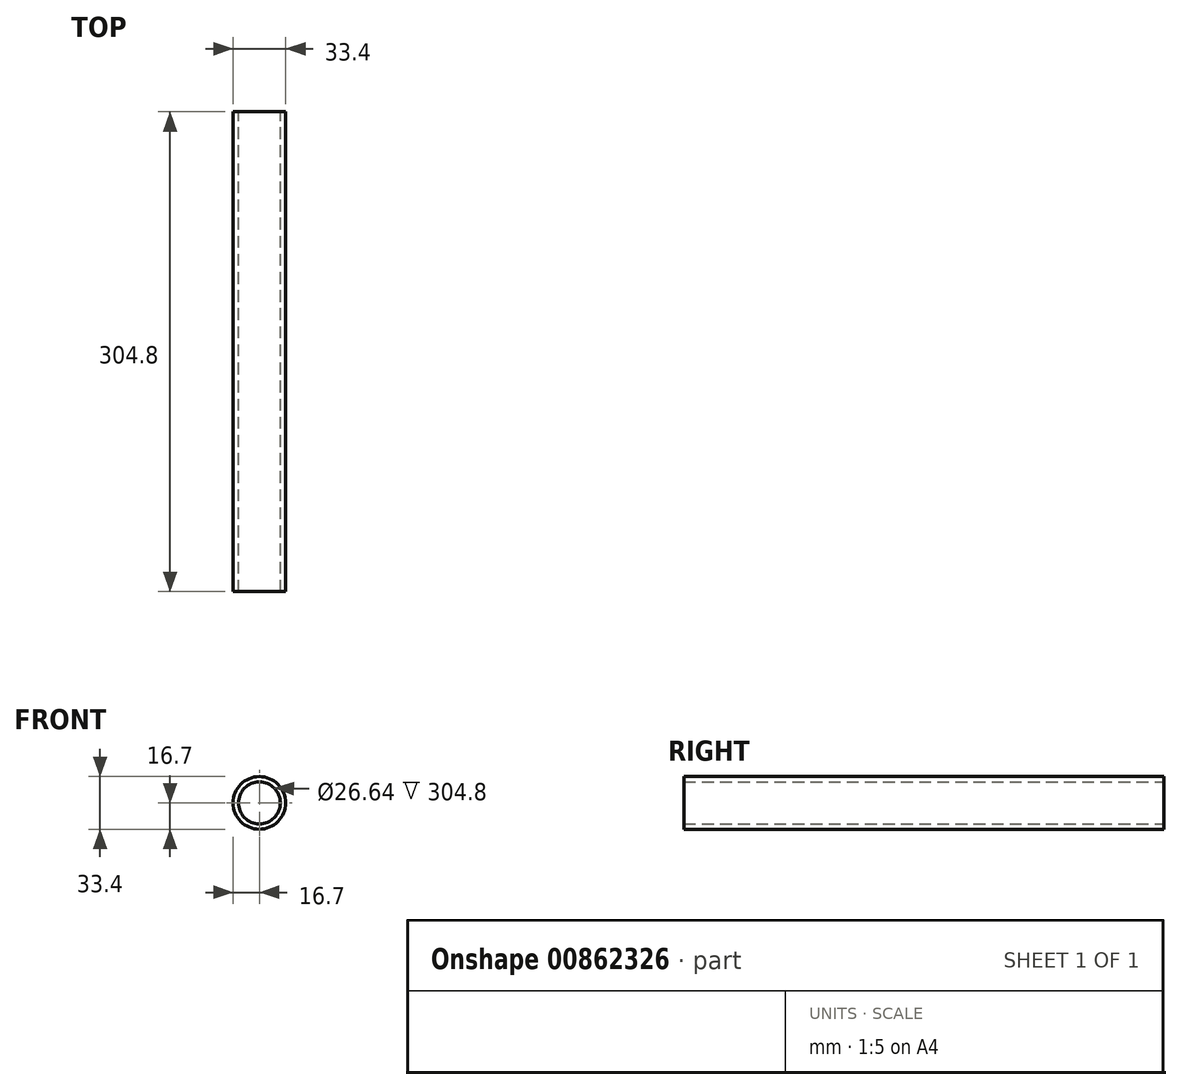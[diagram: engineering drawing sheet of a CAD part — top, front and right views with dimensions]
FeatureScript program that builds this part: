
annotation { "Feature Type Name" : "Feature", "Feature Type Description" : "" }
export const myFeature = defineFeature(function(context is Context, id is Id, definition is map)
    precondition{}
    {
        {
            var Q0;
            Q0=qCreatedBy(makeId("Front.planeOp"),FACE);
            var sketch = newSketch(context, id + "F0", { "sketchPlane" : qUnion([Q0])});
            skCircle(sketch, "E0", {"center": v(0, 0) * mm, "radius": 16.7 * mm});
            skCircle(sketch, "E1", {"center": v(0, 0) * mm, "radius": 13.32 * mm});
            skSolve(sketch);
        }
        {
            var Q0;
            Q0=makeQuery(id+"F0.imprint","IMPRINT",FACE,{"disambiguationData":[TD([[makeQuery(id+"F0.imprint","IMPRINT",EDGE,{"derivedFrom":sQuery(id+"F0.wireOp",EDGE,"E0")}),1.0]])]});
            extrude(context, id + "F1", {"entities" : qUnion([Q0]), "endBound" : BoundingType.SYMMETRIC, "depth" : 304.8 * mm, "offsetDistance" : 25.4 * mm});
        }
        {
            var Q0;
            Q0=qCreatedBy(makeId("Right.planeOp"),FACE);
            var sketch = newSketch(context, id + "F2", { "sketchPlane" : qUnion([Q0])});
            skCircle(sketch, "E2", {"center": v(50.8, 0) * mm, "radius": 4.76 * mm});
            skSolve(sketch);
        }
        {
            var Q0;
            Q0=qCreatedBy(makeId("Right.planeOp"),FACE);
            var sketch = newSketch(context, id + "F3", { "sketchPlane" : qUnion([Q0])});
            skCircle(sketch, "E3", {"center": v(44.7, 50.9) * mm, "radius": 28.47 * mm});
            skSolve(sketch);
        }
        {
            var Q0;
            Q0 = qSketchRegion(id + "F3", true);
            extrude(context, id + "F4", {"entities" : qUnion([Q0]), "depth" : 25.4 * mm, "offsetDistance" : 25.4 * mm});
        }
        {
            var Q0;
            Q0=makeQuery(id+"F4.opExtrude","SWEPT_BODY",BODY,{"disambiguationData":[OSD([sQuery(id+"F3.wireOp",EDGE,"E3")])]});
            deleteBodies(context, id + "F5", {"entities" : qUnion([Q0])});
        }
    });
